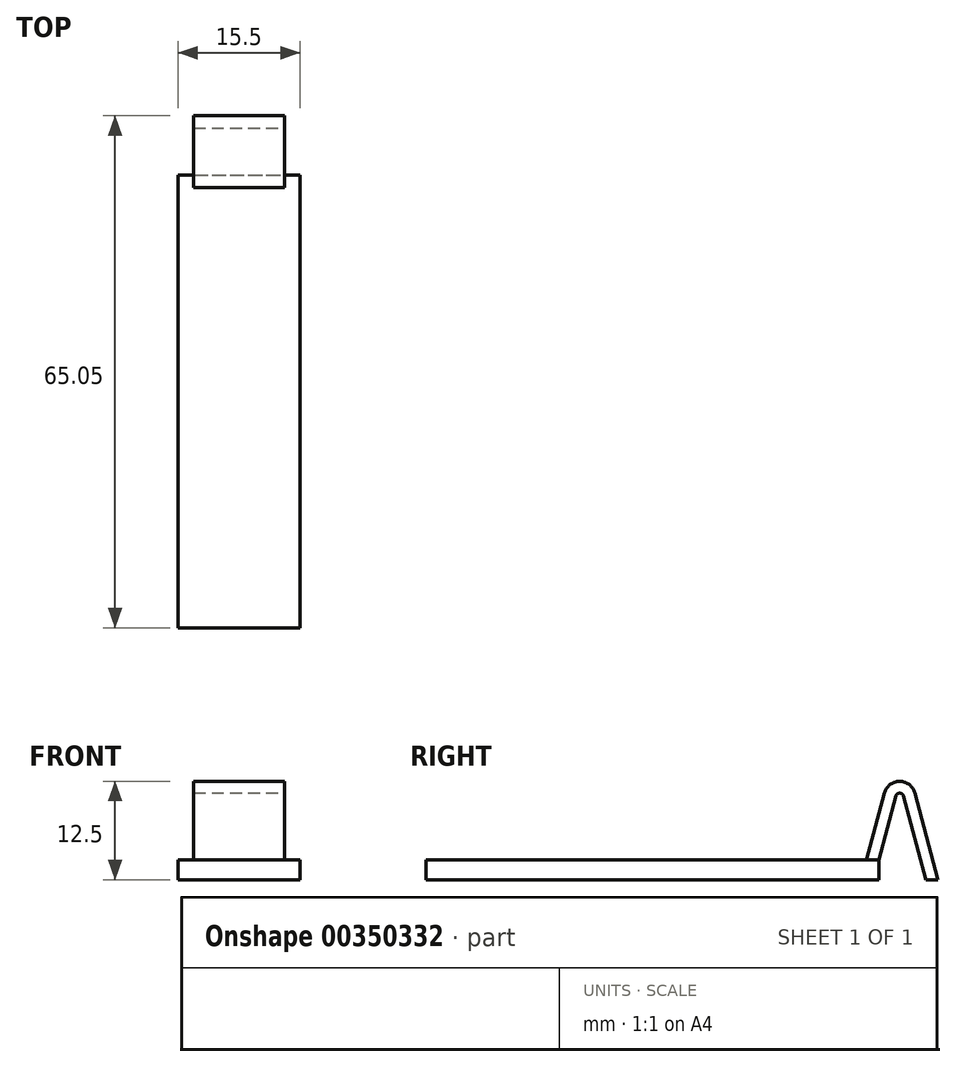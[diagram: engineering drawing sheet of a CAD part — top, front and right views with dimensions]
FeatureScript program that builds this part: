
annotation { "Feature Type Name" : "Feature", "Feature Type Description" : "" }
export const myFeature = defineFeature(function(context is Context, id is Id, definition is map)
    precondition{}
    {
        {
            var Q0;
            Q0=qCreatedBy(makeId("Top.planeOp"),FACE);
            var sketch = newSketch(context, id + "F0", { "sketchPlane" : qUnion([Q0])});
            skLineSegment(sketch, "E0.bottom", {"start": v(0, 0) * mm, "end": v(15.5, 0) * mm});
            skLineSegment(sketch, "E0.top", {"start": v(0, 57.5) * mm, "end": v(15.5, 57.5) * mm});
            skLineSegment(sketch, "E0.left", {"start": v(0, 0) * mm, "end": v(0, 57.5) * mm});
            skLineSegment(sketch, "E0.right", {"start": v(15.5, 0) * mm, "end": v(15.5, 57.5) * mm});
            skSolve(sketch);
        }
        {
            var Q0;
            Q0 = qSketchRegion(id + "F0", true);
            extrude(context, id + "F1", {"entities" : qUnion([Q0]), "depth" : 2.5 * mm});
        }
        {
            var Q0;
            Q0=makeQuery(id+"F1.opExtrude","SWEPT_FACE",FACE,{"disambiguationData":[OSD([sQuery(id+"F0.wireOp",EDGE,"E0.right")])]});
            var sketch = newSketch(context, id + "F2", { "sketchPlane" : qUnion([Q0])});
            skLineSegment(sketch, "E1", {"start": v(57.5, 2.5) * mm, "end": v(59.68, 10.63) * mm});
            skLineSegment(sketch, "E2", {"start": v(60.64, 10.63) * mm, "end": v(63.5, 0) * mm});
            skLineSegment(sketch, "E3", {"start": v(63.5, 0) * mm, "end": v(65.05, 0) * mm});
            skLineSegment(sketch, "E4", {"start": v(65.05, 0) * mm, "end": v(62.1, 11.02) * mm});
            skArc(sketch, "E5", {"start": v(62.1, 11.02) * mm, "mid": v(60.16, 12.5) * mm, "end": v(58.23, 11.02) * mm});
            skLineSegment(sketch, "E6", {"start": v(58.23, 11.02) * mm, "end": v(55.95, 2.5) * mm});
            skArc(sketch, "E7.filletArc", {"start": v(60.64, 10.63) * mm, "mid": v(60.16, 11) * mm, "end": v(59.68, 10.63) * mm});
            skSolve(sketch);
        }
        {
            var Q0;
            {var subQ0=sQuery(id+"F2.wireOp",EDGE,"E1");Q0=makeQuery(id+"F2.imprint","IMPRINT",FACE,{"disambiguationData":[TD([[makeQuery(id+"F2.imprint","IMPRINT",EDGE,{"derivedFrom":subQ0}),1.0]])]});}
            extrude(context, id + "F3", {"entities" : qUnion([Q0]), "operationType" : NewBodyOperationType.ADD, "oppositeDirection" : true, "depth" : 13.5 * mm, "hasSecondDirection" : true, "secondDirectionOppositeDirection" : true, "secondDirectionDepth" : 2 * mm});
        }
    });
